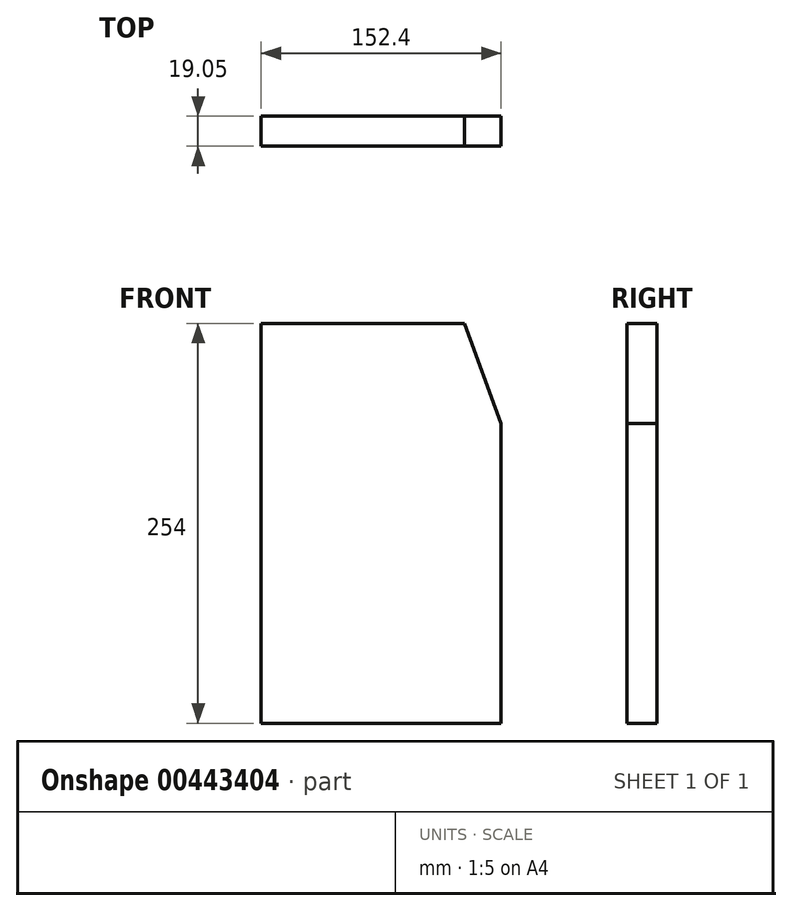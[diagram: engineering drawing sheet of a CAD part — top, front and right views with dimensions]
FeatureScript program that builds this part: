
annotation { "Feature Type Name" : "Feature", "Feature Type Description" : "" }
export const myFeature = defineFeature(function(context is Context, id is Id, definition is map)
    precondition{}
    {
        {
            var Q0;
            Q0=qCreatedBy(makeId("Front.planeOp"),FACE);
            var sketch = newSketch(context, id + "F0", { "sketchPlane" : qUnion([Q0])});
            skLineSegment(sketch, "E0", {"start": v(-71.62, 122.3) * mm, "end": v(-71.62, -131.7) * mm});
            skLineSegment(sketch, "E1", {"start": v(-71.62, -131.7) * mm, "end": v(80.78, -131.7) * mm});
            skLineSegment(sketch, "E2", {"start": v(80.78, -131.7) * mm, "end": v(80.78, 58.8) * mm});
            skLineSegment(sketch, "E3", {"start": v(80.78, 58.8) * mm, "end": v(57.66, 122.3) * mm});
            skLineSegment(sketch, "E4", {"start": v(57.66, 122.3) * mm, "end": v(-71.62, 122.3) * mm});
            skSolve(sketch);
        }
        {
            var Q0;
            Q0 = qSketchRegion(id + "F0", true);
            extrude(context, id + "F1", {"entities" : qUnion([Q0]), "depth" : 19.05 * mm});
        }
    });
